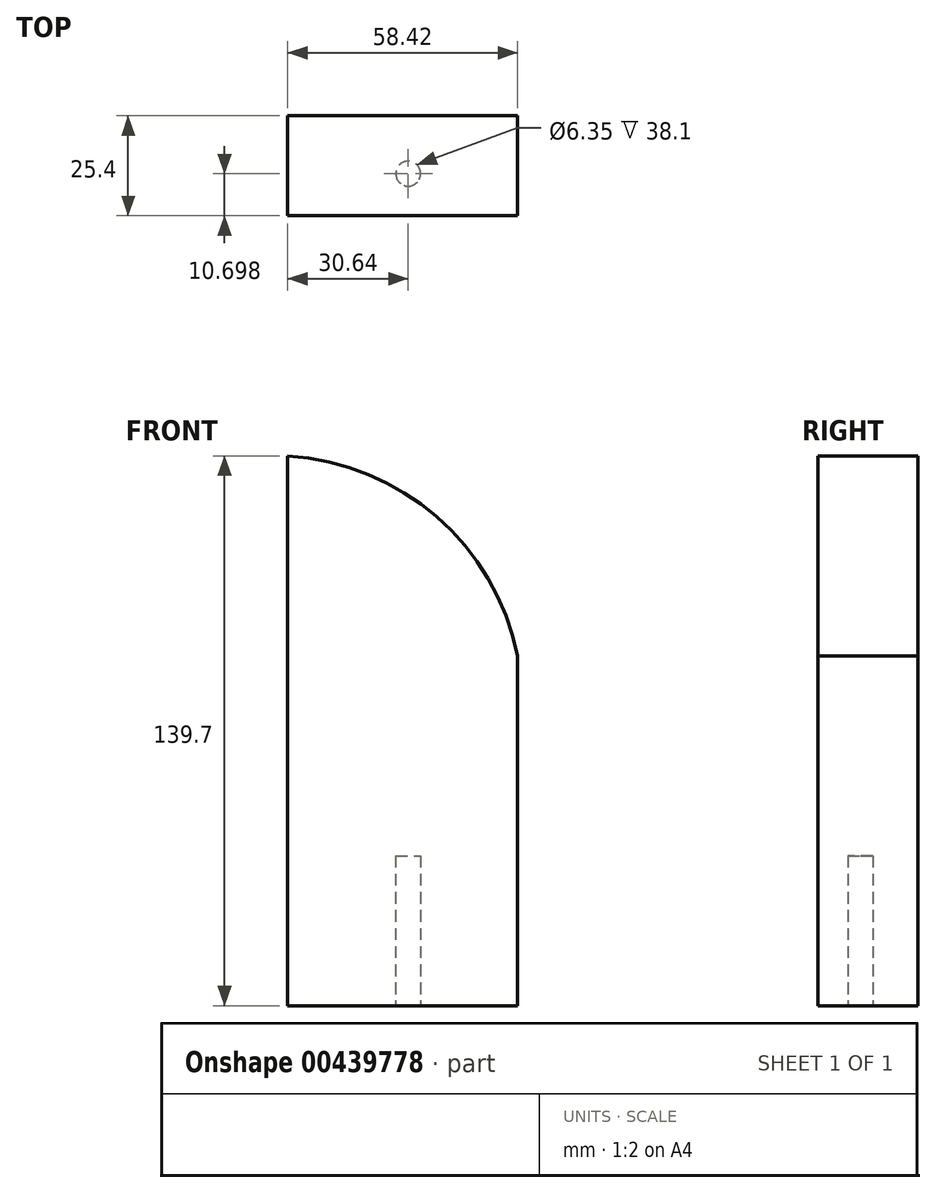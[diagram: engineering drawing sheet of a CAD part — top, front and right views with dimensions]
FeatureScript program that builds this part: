
annotation { "Feature Type Name" : "Feature", "Feature Type Description" : "" }
export const myFeature = defineFeature(function(context is Context, id is Id, definition is map)
    precondition{}
    {
        {
            var Q0;
            Q0=qCreatedBy(makeId("Front.planeOp"),FACE);
            var sketch = newSketch(context, id + "F0", { "sketchPlane" : qUnion([Q0])});
            skLineSegment(sketch, "E0", {"start": v(-30.64, 69.85) * mm, "end": v(-30.64, -69.85) * mm});
            skLineSegment(sketch, "E1", {"start": v(-30.64, -69.85) * mm, "end": v(27.78, -69.85) * mm});
            skLineSegment(sketch, "E2", {"start": v(27.78, -69.85) * mm, "end": v(27.78, 19.05) * mm});
            skArc(sketch, "E3", {"start": v(27.78, 19.05) * mm, "mid": v(7.2, 54.38) * mm, "end": v(-30.64, 69.85) * mm});
            skSolve(sketch);
        }
        {
            var Q0;
            Q0 = qSketchRegion(id + "F0", true);
            extrude(context, id + "F1", {"entities" : qUnion([Q0]), "depth" : 25.4 * mm});
        }
        {
            var Q0;
            Q0=makeQuery(id+"F1.opExtrude","SWEPT_FACE",FACE,{"disambiguationData":[OSD([sQuery(id+"F0.wireOp",EDGE,"E1")])]});
            var sketch = newSketch(context, id + "F2", { "sketchPlane" : qUnion([Q0])});
            skCircle(sketch, "E4", {"center": v(0, 116.44) * mm, "radius": 31.75 * mm});
            skCircle(sketch, "E5", {"center": v(0, 14.7) * mm, "radius": 3.18 * mm});
            skSolve(sketch);
        }
        {
            var Q0;
            Q0 = qSketchRegion(id + "F2", true);
            extrude(context, id + "F3", {"entities" : qUnion([Q0]), "operationType" : NewBodyOperationType.ADD, "depth" : 25.4 * mm});
        }
        {
            var Q0;
            Q0=makeQuery(id+"F3.opExtrude","SWEPT_BODY",BODY,{"disambiguationData":[OSD([sQuery(id+"F2.wireOp",EDGE,"E4")])]});
            deleteBodies(context, id + "F4", {"entities" : qUnion([Q0])});
        }
        {
            var Q0;
            Q0=makeQuery(id+"F3.opExtrude","CAP_FACE",FACE,{"disambiguationData":[OSD([sQuery(id+"F2.wireOp",EDGE,"E5")])],"isStart":false});
            extrude(context, id + "F5", {"entities" : qUnion([Q0]), "operationType" : NewBodyOperationType.REMOVE, "oppositeDirection" : true, "depth" : 12.7 * mm});
        }
        {
            var Q0;
            Q0=makeQuery(id+"F5.boolean.opBoolean","COPY",FACE,{"derivedFrom":makeQuery(id+"F5.opExtrude","CAP_FACE",FACE,{"disambiguationData":[OSD([sQuery(id+"F2.wireOp",EDGE,"E5")])],"isStart":false})});
            extrude(context, id + "F6", {"entities" : qUnion([Q0]), "operationType" : NewBodyOperationType.REMOVE, "oppositeDirection" : true, "depth" : 50.8 * mm});
        }
    });
